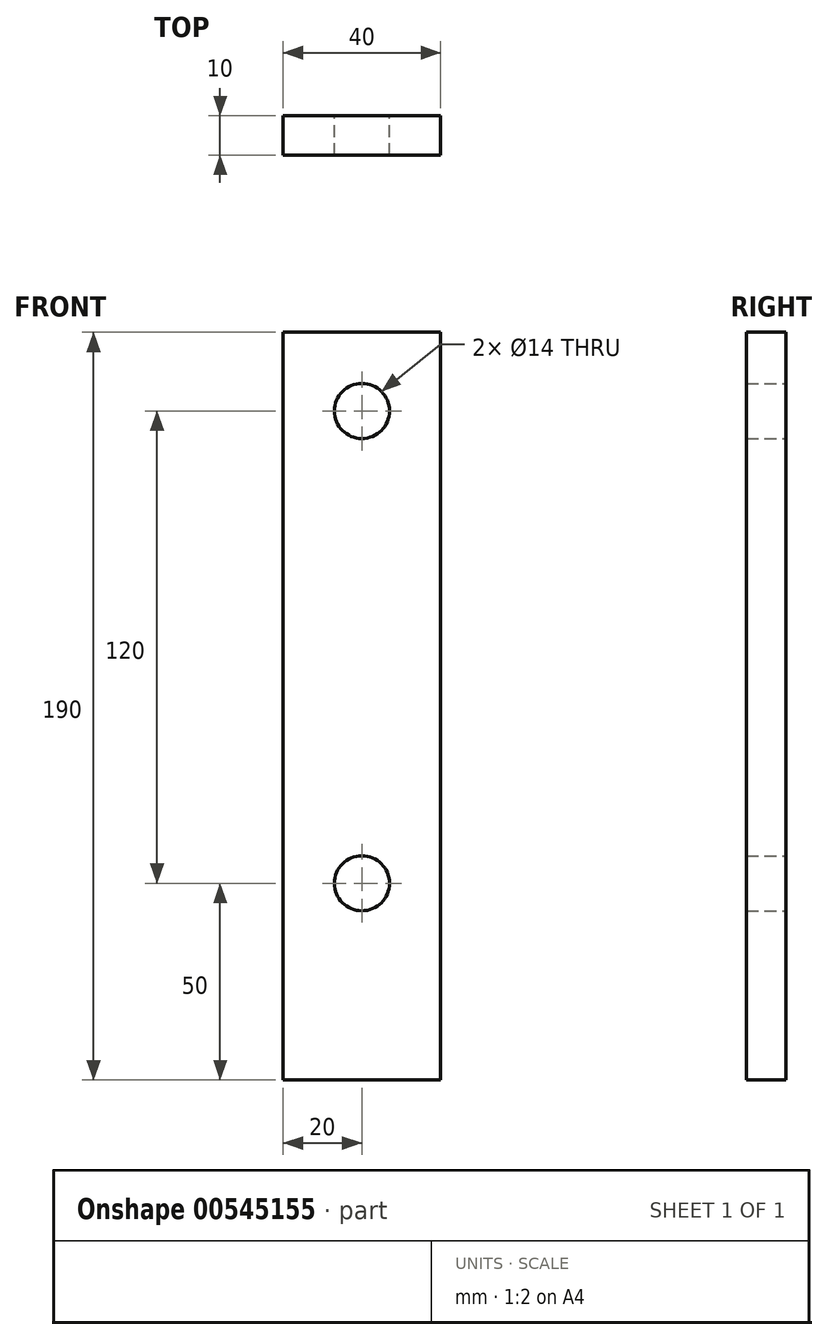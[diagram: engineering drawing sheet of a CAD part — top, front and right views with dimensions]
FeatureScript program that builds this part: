
annotation { "Feature Type Name" : "Feature", "Feature Type Description" : "" }
export const myFeature = defineFeature(function(context is Context, id is Id, definition is map)
    precondition{}
    {
        {
            var Q0;
            Q0=qCreatedBy(makeId("Front.planeOp"),FACE);
            var sketch = newSketch(context, id + "F0", { "sketchPlane" : qUnion([Q0])});
            skLineSegment(sketch, "E0.bottom", {"start": v(-20, 95) * mm, "end": v(20, 95) * mm});
            skLineSegment(sketch, "E0.top", {"start": v(-20, -95) * mm, "end": v(20, -95) * mm});
            skLineSegment(sketch, "E0.left", {"start": v(-20, 95) * mm, "end": v(-20, -95) * mm});
            skLineSegment(sketch, "E0.right", {"start": v(20, 95) * mm, "end": v(20, -95) * mm});
            skPoint(sketch, "E0.middle", {"position": v(0, 0) * mm});
            skCircle(sketch, "E1", {"center": v(0, 75) * mm, "radius": 7 * mm});
            skCircle(sketch, "E2", {"center": v(0, -45) * mm, "radius": 7 * mm});
            skSolve(sketch);
        }
        {
            var Q0;
            Q0=makeQuery(id+"F0.imprint","IMPRINT",FACE,{"disambiguationData":[TD([[makeQuery(id+"F0.imprint","IMPRINT",EDGE,{"derivedFrom":sQuery(id+"F0.wireOp",EDGE,"E0.bottom")}),-1.0]])]});
            extrude(context, id + "F1", {"entities" : qUnion([Q0]), "depth" : 10 * mm, "offsetDistance" : 25 * mm});
        }
    });
